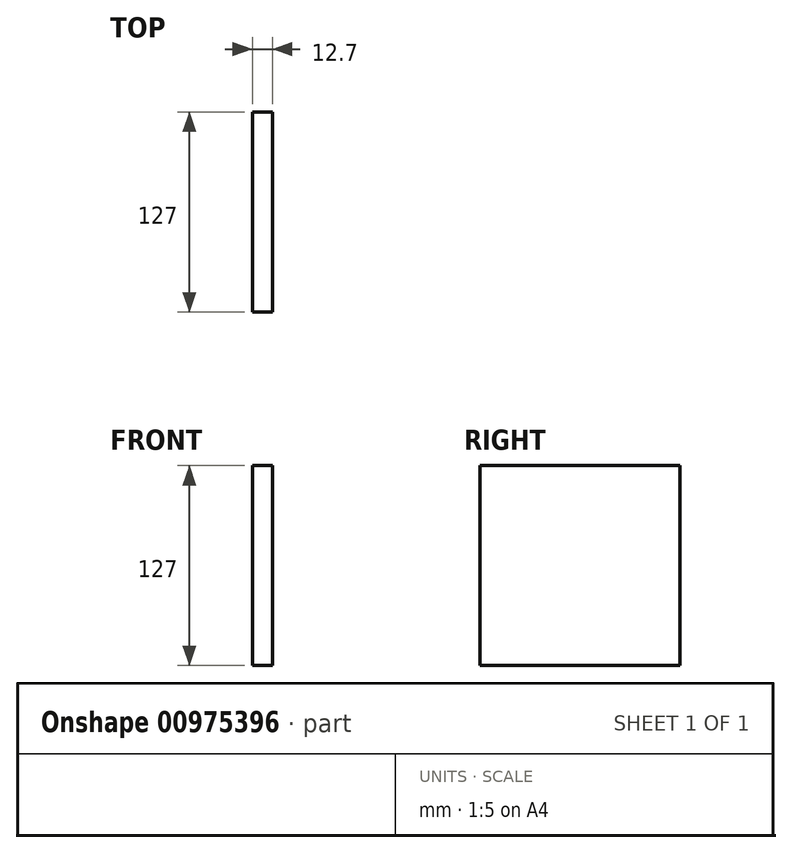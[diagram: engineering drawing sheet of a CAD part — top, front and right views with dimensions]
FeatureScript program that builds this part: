
annotation { "Feature Type Name" : "Feature", "Feature Type Description" : "" }
export const myFeature = defineFeature(function(context is Context, id is Id, definition is map)
    precondition{}
    {
        {
            var Q0;
            Q0=qCreatedBy(makeId("Right.planeOp"),FACE);
            var sketch = newSketch(context, id + "F0", { "sketchPlane" : qUnion([Q0])});
            skLineSegment(sketch, "E0.bottom", {"start": v(-36.31, 56.86) * mm, "end": v(90.69, 56.86) * mm});
            skLineSegment(sketch, "E0.top", {"start": v(-36.31, -70.14) * mm, "end": v(90.69, -70.14) * mm});
            skLineSegment(sketch, "E0.left", {"start": v(-36.31, 56.86) * mm, "end": v(-36.31, -70.14) * mm});
            skLineSegment(sketch, "E0.right", {"start": v(90.69, 56.86) * mm, "end": v(90.69, -70.14) * mm});
            skSolve(sketch);
        }
        {
            var Q0;
            Q0=makeQuery(id+"F0.imprint","IMPRINT",FACE,{"disambiguationData":[TD([[makeQuery(id+"F0.imprint","IMPRINT",EDGE,{"derivedFrom":sQuery(id+"F0.wireOp",EDGE,"E0.bottom")}),-1.0]])]});
            extrude(context, id + "F1", {"entities" : qUnion([Q0]), "depth" : 12.7 * mm, "offsetDistance" : 25.4 * mm});
        }
    });
